FREECAD ASSEMBLY — COMPONENT RECIPES ("Assembly")

This assembly document has 4 components, labeled P0..P3 below (a component is one placed body or linked part). 1 of them carries a construction recipe — the FreeCAD feature program that regenerates the part from scratch, quoted from this document or its linked companion documents; the rest are supplied as boundary geometry only. No exploded tour is included for this assembly.
COMPONENT P0 — recipe-attached ("Hull", a linked part whose construction recipe lives in a companion FreeCAD document of the same project; that document's serialized recipe follows).
Construction recipe (the companion document, serialized — sketch geometry with constraints, then the solid features built on it; lengths are millimeters unless a unit is written):

FCSTD DOCUMENT  (FreeCAD 1.1R40444 (Git))
Label: Hull
License: All rights reserved
LicenseURL: http://en.wikipedia.org/wiki/All_rights_reserved
objects: PartDesign::ShapeBinder×4, PartDesign::Pad×3, Sketcher::SketchObject×2, App::Point×2, PartDesign::Body×2, PartDesign::Pocket×1, PartDesign::Thickness×1
note: 25 computed .brp shape members not serialized (recipe doc carries the construction recipe); baked Part::Feature solids carry a one-line shape summary decoded from their .brp
EXTERNAL_REF file=Configuration.FCStd obj=Spreadsheet

FEATURE [Sketcher::SketchObject] Sketch
  ArcFitTolerance = 0
  AttachmentSupport = -> [XY_Plane]
  ExternalTypes = [0]
  FullyConstrained = false
  MakeInternals = false
  MapMode = 5
  expr: Constraints[4] = 35 mm
  sketch-geometry (4):
    g0: ArcOfCircle CenterX=-25.5208 CenterY=0 CenterZ=0 NormalX=0 NormalY=0 NormalZ=1 AngleXU=0 Radius=16 StartAngle=1.95222 EndAngle=4.33096
    g1: ArcOfCircle CenterX=25.5208 CenterY=0 CenterZ=0 NormalX=0 NormalY=0 NormalZ=1 AngleXU=0 Radius=35 StartAngle=4.33096 EndAngle=8.23541
    g2: LineSegment StartX=-31.4767 StartY=14.8501 StartZ=0 EndX=12.4922 EndY=32.4847 EndZ=0
    g3: LineSegment StartX=-31.4767 StartY=-14.8501 StartZ=0 EndX=12.4922 EndY=-32.4847 EndZ=0
  constraints (8):
    c: Tangent(g0,g2) = 1.5708
    c: Tangent(g0,g3) = -1.5708
    c: Tangent(g1,g2) = 1.5708
    c: Tangent(g1,g3) = -1.5708
    c: Radius(g1) = 35
    c: PointOnObject(g0,g-1)
    c: Symmetric(g0,g1,g-2)
    c: Radius(g0) = 16
FEATURE [PartDesign::ShapeBinder] ShapeBinder
  Support = -> [Sketch]
  Suppressed = false
  TraceSupport = false
FEATURE [PartDesign::Pad] Pad
  Direction = (0,0,1)
  Length = 22
  Length2 = 10
  Profile = -> ShapeBinder
  Refine = true
  Suppressed = false
  Type = 0
  expr: Length = Configuration#Spreadsheet.gear_height + 2
FEATURE [PartDesign::ShapeBinder] ShapeBinder001
  Support = -> [Sketch]
  Suppressed = false
  TraceSupport = false
FEATURE [Sketcher::SketchObject] Sketch001
  ArcFitTolerance = 0
  AttachmentSupport = -> [XY_Plane001]
  ExternalGeometry = -> [ShapeBinder001]
  ExternalTypes = [1]
  FullyConstrained = true
  MakeInternals = false
  MapMode = 5
  sketch-geometry (1):
    g0: Circle CenterX=25.5208 CenterY=0 CenterZ=0 NormalX=0 NormalY=0 NormalZ=1 AngleXU=0 Radius=10
  constraints (2):
    c: Diameter(g0) = 20
    c: Coincident(g-3,g0)
FEATURE [PartDesign::ShapeBinder] ShapeBinder002
  Support = -> [Sketch001]
  Suppressed = false
  TraceSupport = false
FEATURE [PartDesign::Pad] Pad001
  Direction = (0,0,1)
  Length = 2
  Length2 = 10
  Profile = -> ShapeBinder002
  Refine = true
  Suppressed = false
  Type = 0
FEATURE [PartDesign::ShapeBinder] ShapeBinder003
  Support = -> [Sketch001]
  Suppressed = false
  TraceSupport = false
FEATURE [PartDesign::Pad] Pad002
  BaseFeature = -> Pad001
  Direction = (0,0,1)
  Length = 1
  Length2 = 10
  Profile = -> ShapeBinder003
  Refine = true
  Reversed = true
  Suppressed = false
  Type = 0
FEATURE [App::Point] Origin002  label="Origin"
  Role = Origin
FEATURE [App::Point] Origin003  label="Origin"
  Role = Origin
FEATURE [PartDesign::Pocket] Pocket
  BaseFeature = -> Pad002
  Direction = (0,0,-1)
  Length = 5
  Length2 = 5
  Profile = -> Sketch001
  ReferenceAxis = -> Sketch001 [N_Axis]
  Refine = true
  Reversed = true
  Suppressed = false
  Type = 1
FEATURE [PartDesign::Body] Body001  label="Lid"
  AllowCompound = false
  Group = -> [ShapeBinder001,Sketch001,ShapeBinder002,Pad001,ShapeBinder003,Pad002,Pocket]
  Origin = -> Origin001
  Tip = -> Pocket
FEATURE [PartDesign::Thickness] Thickness
  Base = -> Pad [Face6]
  BaseFeature = -> Pad
  Intersection = false
  Join = 0
  Mode = 0
  Refine = true
  Reversed = true
  SupportTransform = false
  Suppressed = false
  Value = 2
  expr: Value = 2
FEATURE [PartDesign::Body] Body  label="Hull"
  AllowCompound = false
  Group = -> [ShapeBinder,Pad,Thickness]
  Origin = -> Origin
  Tip = -> Thickness
COMPONENT P1 — geometry summary ("Lid"; no construction recipe available for this part):
  bounding box: 108.9 x 77.0 x 6.5 mm
  tessellated surface: 1,536 triangles
  volume: 12101 mm^3 (22% of its bounding box)
  symmetry: mirror-symmetric across its y mid-plane
COMPONENT P2 — geometry summary ("MainGear"; no construction recipe available for this part):
  bounding box: 26.6 x 26.0 x 20.8 mm
  tessellated surface: 6,140 triangles
  volume: 8905 mm^3 (62% of its bounding box)
  symmetry: 6-fold rotationally symmetric about the z axis
COMPONENT P3 — geometry summary ("SecondaryGear"; no construction recipe available for this part):
  bounding box: 50.6 x 50.0 x 21.6 mm
  tessellated surface: 10,512 triangles
  volume: 34000 mm^3 (62% of its bounding box)
  symmetry: 2-fold rotationally symmetric about the y axis; mirror-symmetric across its y mid-plane
PROVENANCE & LICENSES
A FreeCAD (.FCStd) document from a public repository crawl; recipes are the document's own serialized feature recipes (and, for linked parts, companion documents' recipes).
License: as declared in the source repository (recorded in the dataset sidecar).
